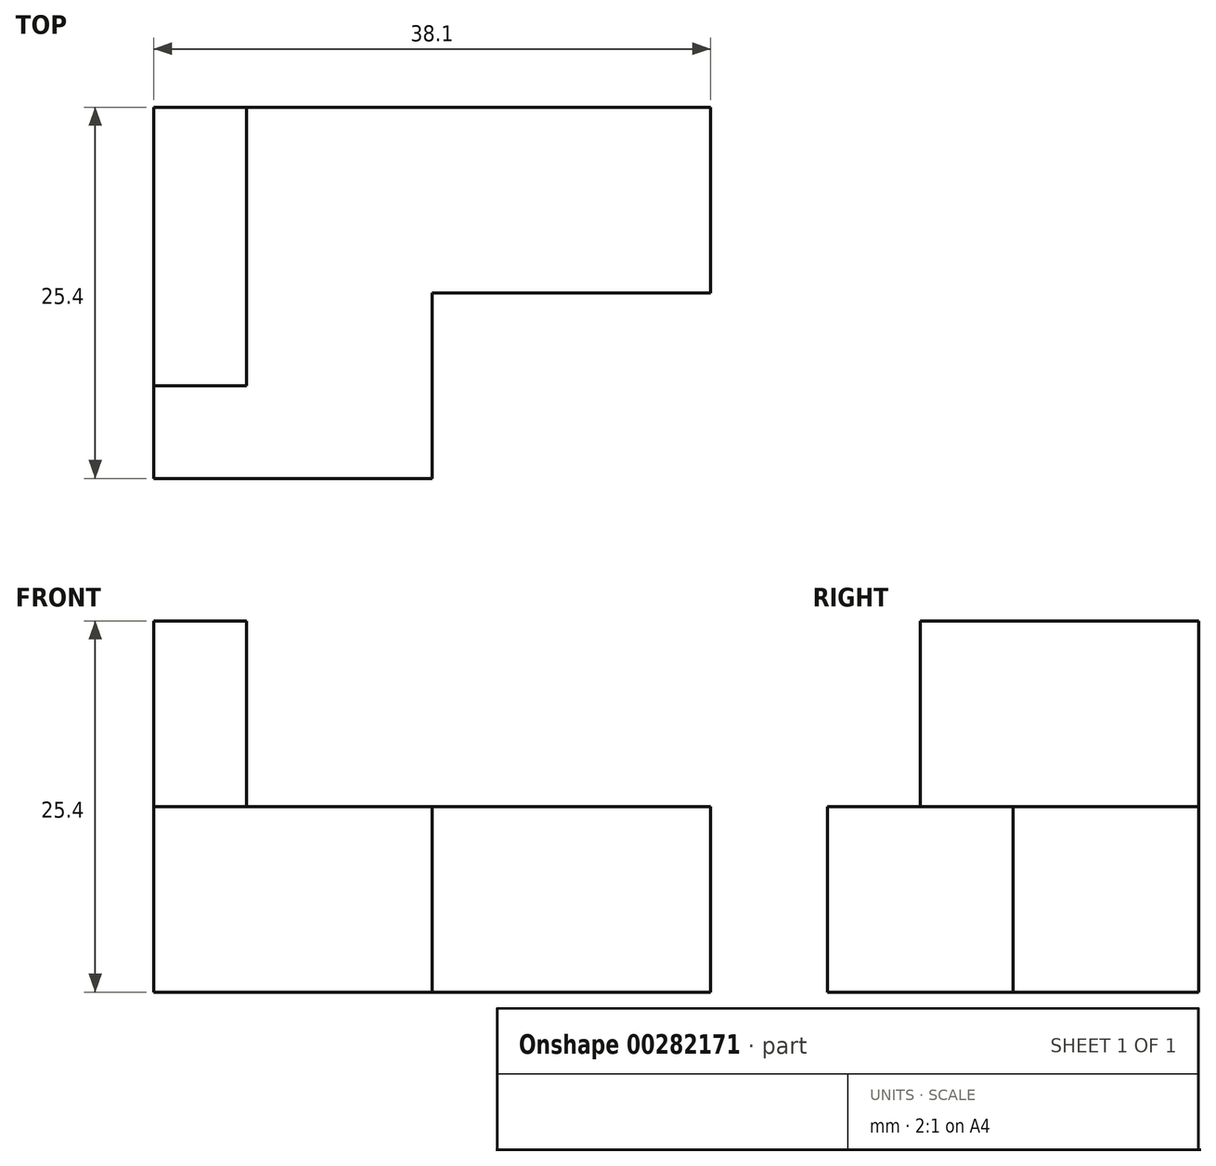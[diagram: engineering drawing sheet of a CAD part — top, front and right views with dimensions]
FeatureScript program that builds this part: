
annotation { "Feature Type Name" : "Feature", "Feature Type Description" : "" }
export const myFeature = defineFeature(function(context is Context, id is Id, definition is map)
    precondition{}
    {
        {
            var Q0;
            Q0=qCreatedBy(makeId("Top.planeOp"),FACE);
            var sketch = newSketch(context, id + "F0", { "sketchPlane" : qUnion([Q0])});
            skLineSegment(sketch, "E0", {"start": v(0, 25.4) * mm, "end": v(38.1, 25.4) * mm});
            skLineSegment(sketch, "E1", {"start": v(38.1, 25.4) * mm, "end": v(38.1, 12.7) * mm});
            skLineSegment(sketch, "E2", {"start": v(38.1, 12.7) * mm, "end": v(19.05, 12.7) * mm});
            skLineSegment(sketch, "E3", {"start": v(19.05, 12.7) * mm, "end": v(19.05, 0) * mm});
            skLineSegment(sketch, "E4", {"start": v(19.05, 0) * mm, "end": v(0, 0) * mm});
            skLineSegment(sketch, "E5", {"start": v(0, 0) * mm, "end": v(0, 25.4) * mm});
            skSolve(sketch);
        }
        {
            var Q0;
            Q0=makeQuery(id+"F0.imprint","IMPRINT",FACE,{"disambiguationData":[TD([[makeQuery(id+"F0.imprint","IMPRINT",EDGE,{"derivedFrom":sQuery(id+"F0.wireOp",EDGE,"E0")}),-1.0]])]});
            extrude(context, id + "F1", {"entities" : qUnion([Q0]), "depth" : 12.7 * mm});
        }
        {
            var Q0;
            Q0=makeQuery(id+"F1.opExtrude","CAP_FACE",FACE,{"disambiguationData":[OSD([sQuery(id+"F0.wireOp",EDGE,"E0"),sQuery(id+"F0.wireOp",EDGE,"E1"),sQuery(id+"F0.wireOp",EDGE,"E2"),sQuery(id+"F0.wireOp",EDGE,"E3"),sQuery(id+"F0.wireOp",EDGE,"E4"),sQuery(id+"F0.wireOp",EDGE,"E5")])],"isStart":false});
            var sketch = newSketch(context, id + "F2", { "sketchPlane" : qUnion([Q0])});
            skSolve(sketch);
        }
        {
            var Q0;
            Q0=makeQuery(id+"F2.imprint","IMPRINT",FACE,{"disambiguationData":[TD([[makeQuery(id+"F2.imprint","IMPRINT",EDGE,{"derivedFrom":makeQuery(id+"F1.opExtrude","CAP_EDGE",EDGE,{"disambiguationData":[OSD([sQuery(id+"F0.wireOp",EDGE,"E0")])],"isStart":false})}),-1.0]])]});
            var sketch = newSketch(context, id + "F3", { "sketchPlane" : qUnion([Q0])});
            skLineSegment(sketch, "E6", {"start": v(0, 6.35) * mm, "end": v(0, 25.4) * mm});
            skLineSegment(sketch, "E7", {"start": v(6.35, 25.4) * mm, "end": v(6.35, 6.35) * mm});
            skLineSegment(sketch, "E8", {"start": v(6.35, 25.4) * mm, "end": v(0, 25.4) * mm});
            skLineSegment(sketch, "E9", {"start": v(0, 6.35) * mm, "end": v(6.35, 6.35) * mm});
            skSolve(sketch);
        }
        {
            var Q0;
            Q0=makeQuery(id+"F3.imprint","IMPRINT",FACE,{"disambiguationData":[TD([[makeQuery(id+"F3.imprint","IMPRINT",EDGE,{"derivedFrom":sQuery(id+"F3.wireOp",EDGE,"E6")}),-1.0]])]});
            extrude(context, id + "F4", {"entities" : qUnion([Q0]), "operationType" : NewBodyOperationType.ADD, "depth" : 12.7 * mm});
        }
    });
